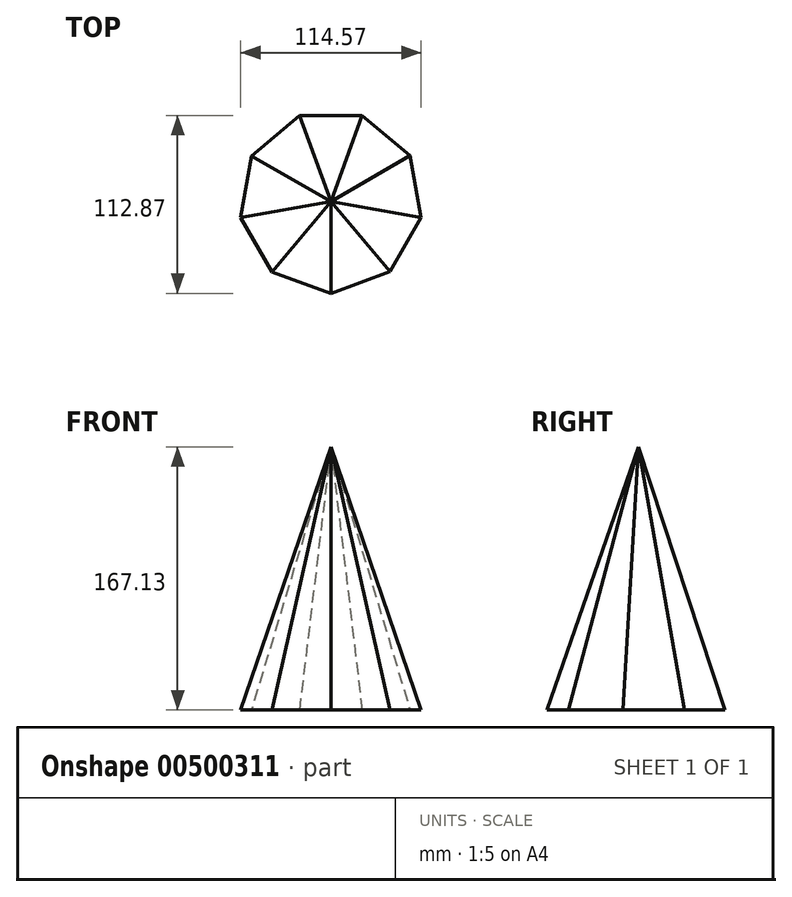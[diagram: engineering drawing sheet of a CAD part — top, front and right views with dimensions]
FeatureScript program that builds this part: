
annotation { "Feature Type Name" : "Feature", "Feature Type Description" : "" }
export const myFeature = defineFeature(function(context is Context, id is Id, definition is map)
    precondition{}
    {
        {
            var Q0;
            Q0=qCreatedBy(makeId("Top.planeOp"),FACE);
            var sketch = newSketch(context, id + "F0", { "sketchPlane" : qUnion([Q0])});
            skCircle(sketch, "E0.cCircle", {"center": v(0, 0) * mm, "radius": 58.17 * mm, "construction": true});
            skLineSegment(sketch, "E0.0", {"start": v(-50.43, 29) * mm, "end": v(-19.99, 54.63) * mm});
            skLineSegment(sketch, "E0.1", {"start": v(-19.99, 54.63) * mm, "end": v(19.8, 54.7) * mm});
            skLineSegment(sketch, "E0.2", {"start": v(19.8, 54.7) * mm, "end": v(50.33, 29.17) * mm});
            skLineSegment(sketch, "E0.3", {"start": v(50.33, 29.17) * mm, "end": v(57.3, -10) * mm});
            skLineSegment(sketch, "E0.4", {"start": v(57.3, -10) * mm, "end": v(37.47, -44.5) * mm});
            skLineSegment(sketch, "E0.5", {"start": v(37.47, -44.5) * mm, "end": v(0.1, -58.17) * mm});
            skLineSegment(sketch, "E0.6", {"start": v(0.1, -58.17) * mm, "end": v(-37.32, -44.62) * mm});
            skLineSegment(sketch, "E0.7", {"start": v(-37.32, -44.62) * mm, "end": v(-57.27, -10.2) * mm});
            skLineSegment(sketch, "E0.8", {"start": v(-57.27, -10.2) * mm, "end": v(-50.43, 29) * mm});
            skSolve(sketch);
        }
        {
            var Q0;
            Q0=qCreatedBy(makeId("Top.planeOp"),FACE);
            cPlane(context, id + "F1", {"entities" : qUnion([Q0]), "cplaneType" : CPlaneType.OFFSET, "offset" : 167.13 * mm, "width" : 152.4 * mm, "height" : 152.4 * mm});
        }
        {
            var Q0;
            Q0=qCreatedBy(id+"F1.planeOp",FACE);
            var sketch = newSketch(context, id + "F2", { "sketchPlane" : qUnion([Q0])});
            skPoint(sketch, "E1", {"position": v(0, 0) * mm});
            skSolve(sketch);
        }
        {
            var Q0;
            Q0=sQuery(id+"F2.wireOp",VERTEX,"E1");
            var Q1;
            Q1=makeQuery(id+"F0.imprint","IMPRINT",FACE,{"disambiguationData":[TD([[makeQuery(id+"F0.imprint","IMPRINT",EDGE,{"derivedFrom":sQuery(id+"F0.wireOp",EDGE,"E0.0")}),-1.0]])]});
            loft(context, id + "F3", {"sheetProfilesArray" : [{ "sheetProfileEntities" : qUnion([Q0]) }, { "sheetProfileEntities" : qUnion([Q1]) }]});
        }
    });
